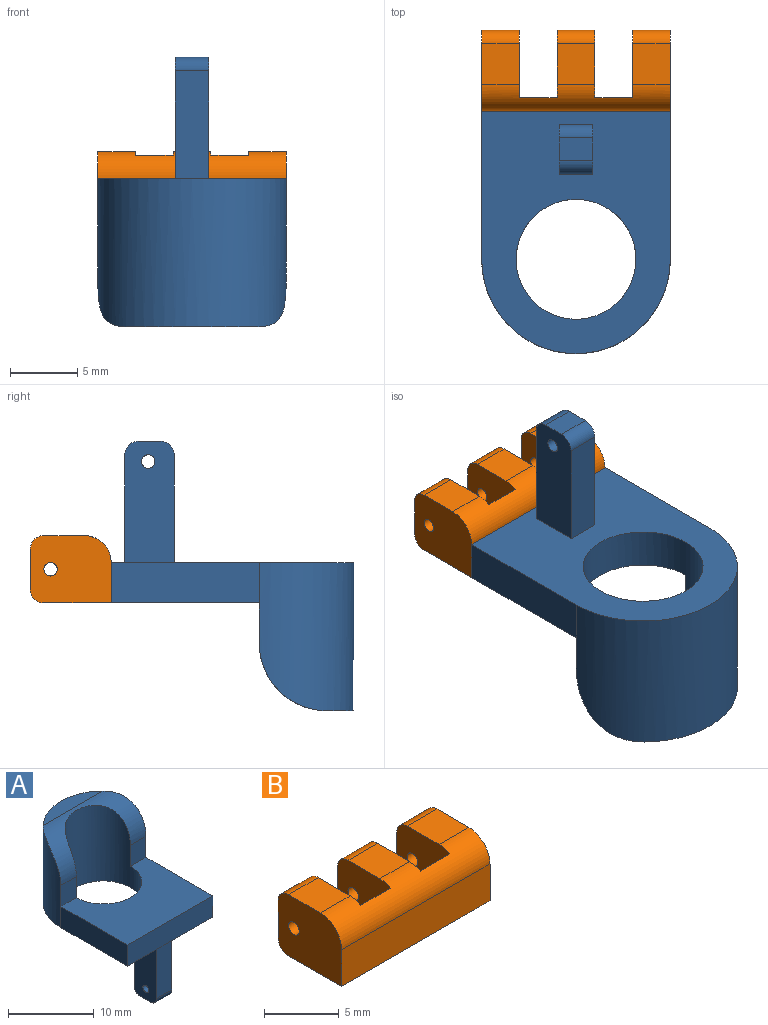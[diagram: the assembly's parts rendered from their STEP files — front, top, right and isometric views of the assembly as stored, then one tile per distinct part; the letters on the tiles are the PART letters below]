
ASSEMBLY  parts=2 mates=1
PART A: 19 faces, bbox 14x18x20 mm
  f0: plane 11x3mm, normal (-1,0,0), area 33mm2, adj f1,f4,f5,f8
  f1: plane 14x3mm, normal (0,-1,0), area 42mm2, adj f0,f2,f4,f5
  f2: plane 11x3mm, normal (1,0,0), area 33mm2, adj f1,f4,f5,f8
  f3: cylinder r=4.45mm len=10.97mm, axis (0,0,-1), area 184.1mm2, adj f4,f5,f6,f7,f18
  f4: plane 14x11mm, normal (0,0,1), area 122.9mm2, adj f0,f1,f2,f3,f6,f7
  f5: plane 18x14mm, normal (0,0,-1), area 159.6mm2, adj f0,f1,f2,f3,f8,f11,f12,f13
  f6: plane 3x2.55mm, normal (0,-1,0), area 7.7mm2, adj f3,f4,f8,f18
  f7: plane 3x2.55mm, normal (0,-1,0), area 7.7mm2, adj f3,f4,f8,f18
  f8: cylinder r=7mm len=14mm, axis (0,0,-1), area 230.9mm2, adj f0,f2,f5,f6,f7,f9,f18
  f9: plane 9.8x2mm, normal (0,0,1), area 13.5mm2, adj f8,f18
  f10: plane 2.5x1.68mm, normal (0,0,-1), area 4.2mm2, adj f11,f13,f16,f17
  f11: plane 9x3.68mm, normal (-1,0,0), area 31.9mm2, adj f5,f10,f12,f14,f15,f16,f17
  f12: plane 8x2.5mm, normal (0,1,0), area 20mm2, adj f5,f11,f13,f17
  f13: plane 9x3.68mm, normal (1,0,0), area 31.9mm2, adj f5,f10,f12,f14,f15,f16,f17
  f14: plane 8x2.5mm, normal (0,-1,0), area 20mm2, adj f5,f11,f13,f16
  f15: cylinder r=0.5mm len=2.5mm, axis (-1,0,0), area 7.9mm2, adj f11,f13
  f16: cylinder r=1mm len=2.5mm, axis (1,0,0), area 3.9mm2, adj f10,f11,f13,f14
  f17: cylinder r=1mm len=2.5mm, axis (-1,0,0), area 3.9mm2, adj f10,f11,f12,f13
  f18: cylinder r=5mm len=14mm, axis (-1,0,0), area 47.2mm2, adj f3,f6,f7,f8,f9
PART B: 26 faces, bbox 14x6x5 mm
  f0: plane 3x2.8mm, normal (0,0,1), area 8.4mm2, adj f11,f13,f19,f25
  f1: plane 3x2.8mm, normal (0,0,1), area 8.4mm2, adj f7,f9,f20,f25
  f2: plane 14x3mm, normal (0,-1,0), area 42mm2, adj f3,f13,f15,f25
  f3: plane 6x5mm, normal (1,0,0), area 27.9mm2, adj f2,f4,f14,f15,f18,f21,f24,f25
  f4: plane 3x2.8mm, normal (0,1,0), area 8.4mm2, adj f3,f5,f18,f21
  f5: plane 5x5mm, normal (-1,0,0), area 23.7mm2, adj f4,f6,f14,f15,f18,f21,f24,f25
  f6: plane 4.73x2.8mm, normal (0,1,0), area 13.2mm2, adj f5,f7,f15,f25
  f7: plane 5x5mm, normal (1,0,0), area 23.7mm2, adj f1,f6,f8,f15,f17,f20,f23,f25
  f8: plane 3x2.8mm, normal (0,1,0), area 8.4mm2, adj f7,f9,f17,f20
  f9: plane 5x5mm, normal (-1,0,0), area 23.7mm2, adj f1,f8,f10,f15,f17,f20,f23,f25
  f10: plane 4.73x2.8mm, normal (0,1,0), area 13.2mm2, adj f9,f11,f15,f25
  f11: plane 5x5mm, normal (1,0,0), area 23.7mm2, adj f0,f10,f12,f15,f16,f19,f22,f25
  f12: plane 3x2.8mm, normal (0,1,0), area 8.4mm2, adj f11,f13,f16,f19
  f13: plane 6x5mm, normal (-1,0,0), area 27.9mm2, adj f0,f2,f12,f15,f16,f19,f22,f25
  f14: plane 3x2.8mm, normal (0,0,1), area 8.4mm2, adj f3,f5,f21,f25
  f15: plane 14x5mm, normal (0,0,-1), area 47.6mm2, adj f2,f3,f5,f6,f7,f9,f10,f11
  f16: cylinder r=1mm len=2.8mm, axis (-1,0,0), area 4.4mm2, adj f11,f12,f13,f15
  f17: cylinder r=1mm len=2.8mm, axis (-1,0,0), area 4.4mm2, adj f7,f8,f9,f15
  f18: cylinder r=1mm len=2.8mm, axis (-1,0,0), area 4.4mm2, adj f3,f4,f5,f15
  f19: cylinder r=1mm len=2.8mm, axis (1,0,0), area 4.4mm2, adj f0,f11,f12,f13
  f20: cylinder r=1mm len=2.8mm, axis (1,0,0), area 4.4mm2, adj f1,f7,f8,f9
  f21: cylinder r=1mm len=2.8mm, axis (1,0,0), area 4.4mm2, adj f3,f4,f5,f14
  f22: cylinder r=0.5mm len=2.8mm, axis (1,0,0), area 8.8mm2, adj f11,f13
  f23: cylinder r=0.5mm len=2.8mm, axis (1,0,0), area 8.8mm2, adj f7,f9
  f24: cylinder r=0.5mm len=2.8mm, axis (1,0,0), area 8.8mm2, adj f3,f5
  f25: cylinder r=2mm len=14mm, axis (-1,0,0), area 38.1mm2, adj f0,f1,f2,f3,f5,f6,f7,f9
PLACE A rot(axis=(1,0,0),180deg) t=(-5.03,-15.57,2.5)mm
PLACE B t=(-4.06,-4.57,-0.5)mm
MATE fastened A.f1 <-> B.f2  axis (0,1,0) through (-5.03,-4.57,1)mm
